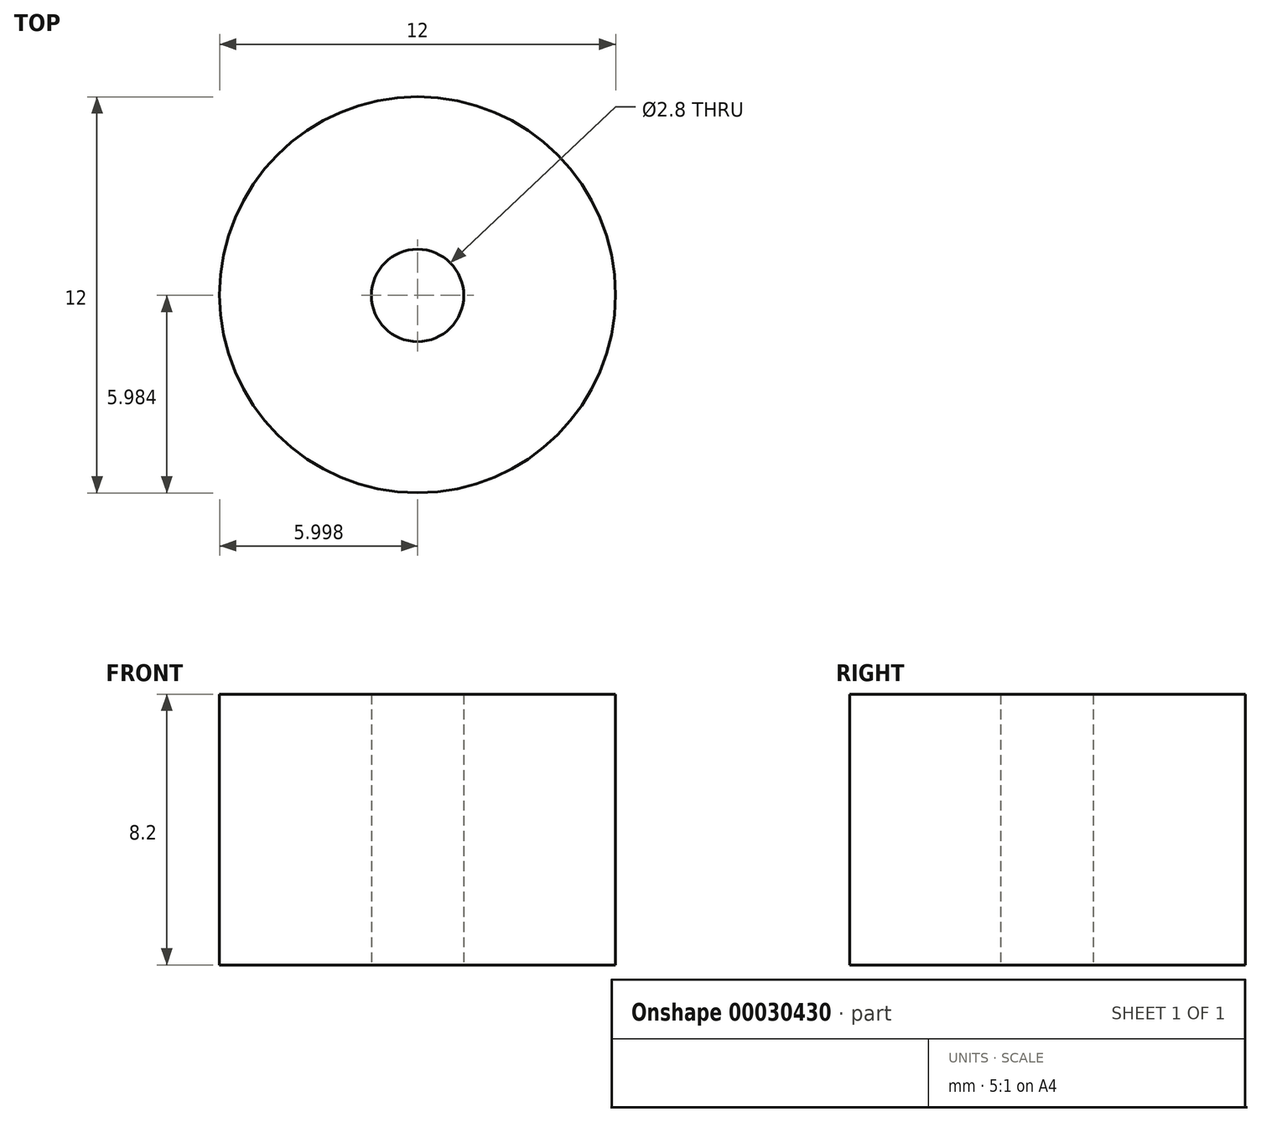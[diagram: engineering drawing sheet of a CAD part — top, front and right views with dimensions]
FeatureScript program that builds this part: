
annotation { "Feature Type Name" : "Feature", "Feature Type Description" : "" }
export const myFeature = defineFeature(function(context is Context, id is Id, definition is map)
    precondition{}
    {
        {
            var Q0;
            Q0=qCreatedBy(makeId("Top.planeOp"),FACE);
            var sketch = newSketch(context, id + "F0", { "sketchPlane" : qUnion([Q0])});
            skCircle(sketch, "E0", {"center": v(-28.72, 20.67) * mm, "radius": 6 * mm});
            skSolve(sketch);
        }
        {
            var Q0;
            Q0=makeQuery(id+"F0.imprint","IMPRINT",FACE,{"disambiguationData":[TD([[makeQuery(id+"F0.imprint","IMPRINT",EDGE,{"derivedFrom":sQuery(id+"F0.wireOp",EDGE,"E0")}),1.0]])]});
            var sketch = newSketch(context, id + "F1", { "sketchPlane" : qUnion([Q0])});
            skCircle(sketch, "E1", {"center": v(-28.72, 20.65) * mm, "radius": 1.4 * mm});
            skSolve(sketch);
        }
        {
            var Q0;
            Q0=makeQuery(id+"F0.imprint","IMPRINT",FACE,{"disambiguationData":[TD([[makeQuery(id+"F0.imprint","IMPRINT",EDGE,{"derivedFrom":sQuery(id+"F0.wireOp",EDGE,"E0")}),1.0]])]});
            extrude(context, id + "F2", {"entities" : qUnion([Q0]), "depth" : 8.2 * mm});
        }
        {
            var Q0;
            Q0 = qSketchRegion(id + "F1", true);
            extrude(context, id + "F3", {"entities" : qUnion([Q0]), "operationType" : NewBodyOperationType.REMOVE, "depth" : 25 * mm});
        }
    });
